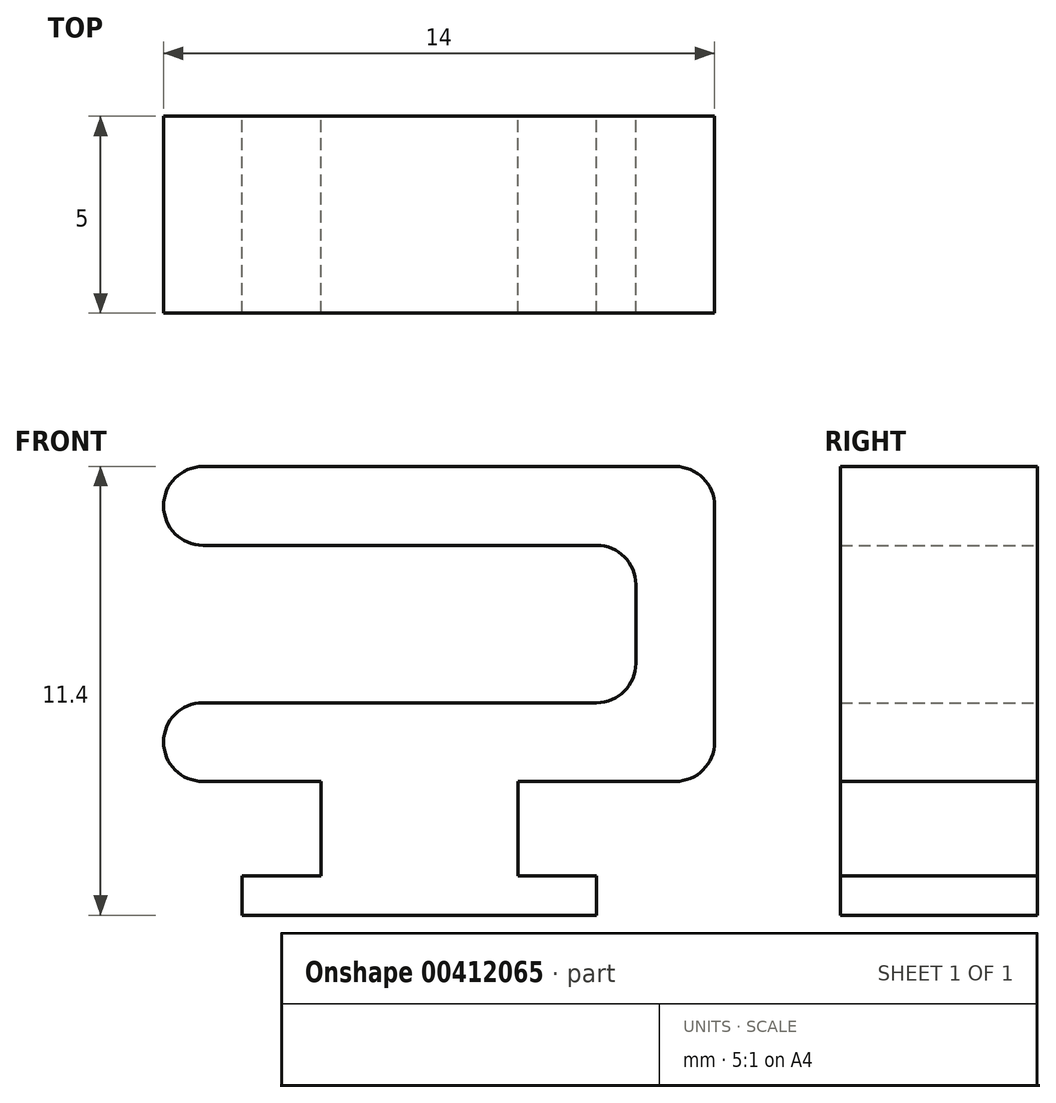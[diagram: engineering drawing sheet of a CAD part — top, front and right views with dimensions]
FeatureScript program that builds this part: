
annotation { "Feature Type Name" : "Feature", "Feature Type Description" : "" }
export const myFeature = defineFeature(function(context is Context, id is Id, definition is map)
    precondition{}
    {
        {
            var Q0;
            Q0=qCreatedBy(makeId("Front.planeOp"),FACE);
            var sketch = newSketch(context, id + "F0", { "sketchPlane" : qUnion([Q0])});
            skLineSegment(sketch, "E0", {"start": v(0, 0) * mm, "end": v(0, -2.4) * mm});
            skLineSegment(sketch, "E1", {"start": v(0, -2.4) * mm, "end": v(-2, -2.4) * mm});
            skPoint(sketch, "E2", {"position": v(2.5, 0) * mm});
            skLineSegment(sketch, "E3", {"start": v(2.5, 8.72) * mm, "end": v(2.5, -16.21) * mm, "construction": true});
            skLineSegment(sketch, "E4", {"start": v(-2, -2.4) * mm, "end": v(-2, -3.4) * mm});
            skLineSegment(sketch, "E5.MirrorCS", {"start": v(5, 0) * mm, "end": v(5, -2.4) * mm});
            skLineSegment(sketch, "E6.MirrorCS", {"start": v(5, -2.4) * mm, "end": v(7, -2.4) * mm});
            skLineSegment(sketch, "E7.MirrorCS", {"start": v(7, -2.4) * mm, "end": v(7, -3.4) * mm});
            skLineSegment(sketch, "E8", {"start": v(-2, -3.4) * mm, "end": v(7, -3.4) * mm});
            skLineSegment(sketch, "E9.bottom", {"start": v(5, 0) * mm, "end": v(10, 0) * mm});
            skLineSegment(sketch, "E10.right", {"start": v(8, 2) * mm, "end": v(8, 6) * mm});
            skLineSegment(sketch, "E11.bottom", {"start": v(8, 6) * mm, "end": v(-4, 6) * mm});
            skLineSegment(sketch, "E11.top", {"start": v(10, 8) * mm, "end": v(-4, 8) * mm});
            skLineSegment(sketch, "E11.right", {"start": v(-4, 6) * mm, "end": v(-4, 8) * mm});
            skPoint(sketch, "E12.end.orphan", {"position": v(5, 0) * mm});
            skLineSegment(sketch, "E13", {"start": v(-4, 2) * mm, "end": v(8, 2) * mm});
            skLineSegment(sketch, "E14", {"start": v(10, 0) * mm, "end": v(10, 8) * mm});
            skLineSegment(sketch, "E15", {"start": v(0, 0) * mm, "end": v(-4, 0) * mm});
            skLineSegment(sketch, "E16", {"start": v(-4, 2) * mm, "end": v(-4, 0) * mm});
            skSolve(sketch);
        }
        {
            var Q0;
            Q0=makeQuery(id+"F0.imprint","IMPRINT",FACE,{"disambiguationData":[TD([[makeQuery(id+"F0.imprint","IMPRINT",EDGE,{"derivedFrom":sQuery(id+"F0.wireOp",EDGE,"E0")}),1.0]])]});
            extrude(context, id + "F1", {"entities" : qUnion([Q0]), "depth" : 5 * mm});
        }
        {
            var Q0;
            Q0=makeQuery(id+"F1.opExtrude","SWEPT_EDGE",EDGE,{"disambiguationData":[OSD([sQuery(id+"F0.wireOp",EDGE,"E10.right"),sQuery(id+"F0.wireOp",EDGE,"E11.bottom")])]});
            var Q1;
            Q1=makeQuery(id+"F1.opExtrude","SWEPT_EDGE",EDGE,{"disambiguationData":[OSD([sQuery(id+"F0.wireOp",EDGE,"E10.right"),sQuery(id+"F0.wireOp",EDGE,"E13")])]});
            var Q2;
            Q2=makeQuery(id+"F1.opExtrude","SWEPT_EDGE",EDGE,{"disambiguationData":[OSD([sQuery(id+"F0.wireOp",EDGE,"E9.bottom"),sQuery(id+"F0.wireOp",EDGE,"E14")])]});
            var Q3;
            Q3=makeQuery(id+"F1.opExtrude","SWEPT_EDGE",EDGE,{"disambiguationData":[OSD([sQuery(id+"F0.wireOp",EDGE,"E11.top"),sQuery(id+"F0.wireOp",EDGE,"E14")])]});
            var Q4;
            Q4=makeQuery(id+"F1.opExtrude","SWEPT_EDGE",EDGE,{"disambiguationData":[OSD([sQuery(id+"F0.wireOp",EDGE,"E11.top"),sQuery(id+"F0.wireOp",EDGE,"E11.right")])]});
            var Q5;
            Q5=makeQuery(id+"F1.opExtrude","SWEPT_EDGE",EDGE,{"disambiguationData":[OSD([sQuery(id+"F0.wireOp",EDGE,"E11.bottom"),sQuery(id+"F0.wireOp",EDGE,"E11.right")])]});
            var Q6;
            Q6=makeQuery(id+"F1.opExtrude","SWEPT_EDGE",EDGE,{"disambiguationData":[OSD([sQuery(id+"F0.wireOp",EDGE,"Gjhbbw6W-1qVI-5eia-6jKN-hLhQOjz80dcH.right"),sQuery(id+"F0.wireOp",EDGE,"E13")])]});
            var Q7;
            Q7=makeQuery(id+"F1.opExtrude","SWEPT_EDGE",EDGE,{"disambiguationData":[OSD([sQuery(id+"F0.wireOp",EDGE,"Gjhbbw6W-1qVI-5eia-6jKN-hLhQOjz80dcH.bottom"),sQuery(id+"F0.wireOp",EDGE,"Gjhbbw6W-1qVI-5eia-6jKN-hLhQOjz80dcH.right")])]});
            var Q8;
            Q8=makeQuery(id+"F1.opExtrude","SWEPT_EDGE",EDGE,{"disambiguationData":[OSD([sQuery(id+"F0.wireOp",EDGE,"E15"),sQuery(id+"F0.wireOp",EDGE,"E16")])]});
            fillet(context, id + "F2", {"entities" : qUnion([Q0, Q1, Q2, Q3, Q4, Q5, Q6, Q7, Q8]), "radius" : 1 * mm, "tangentPropagation" : true, "allowEdgeOverflow" : false});
        }
    });
